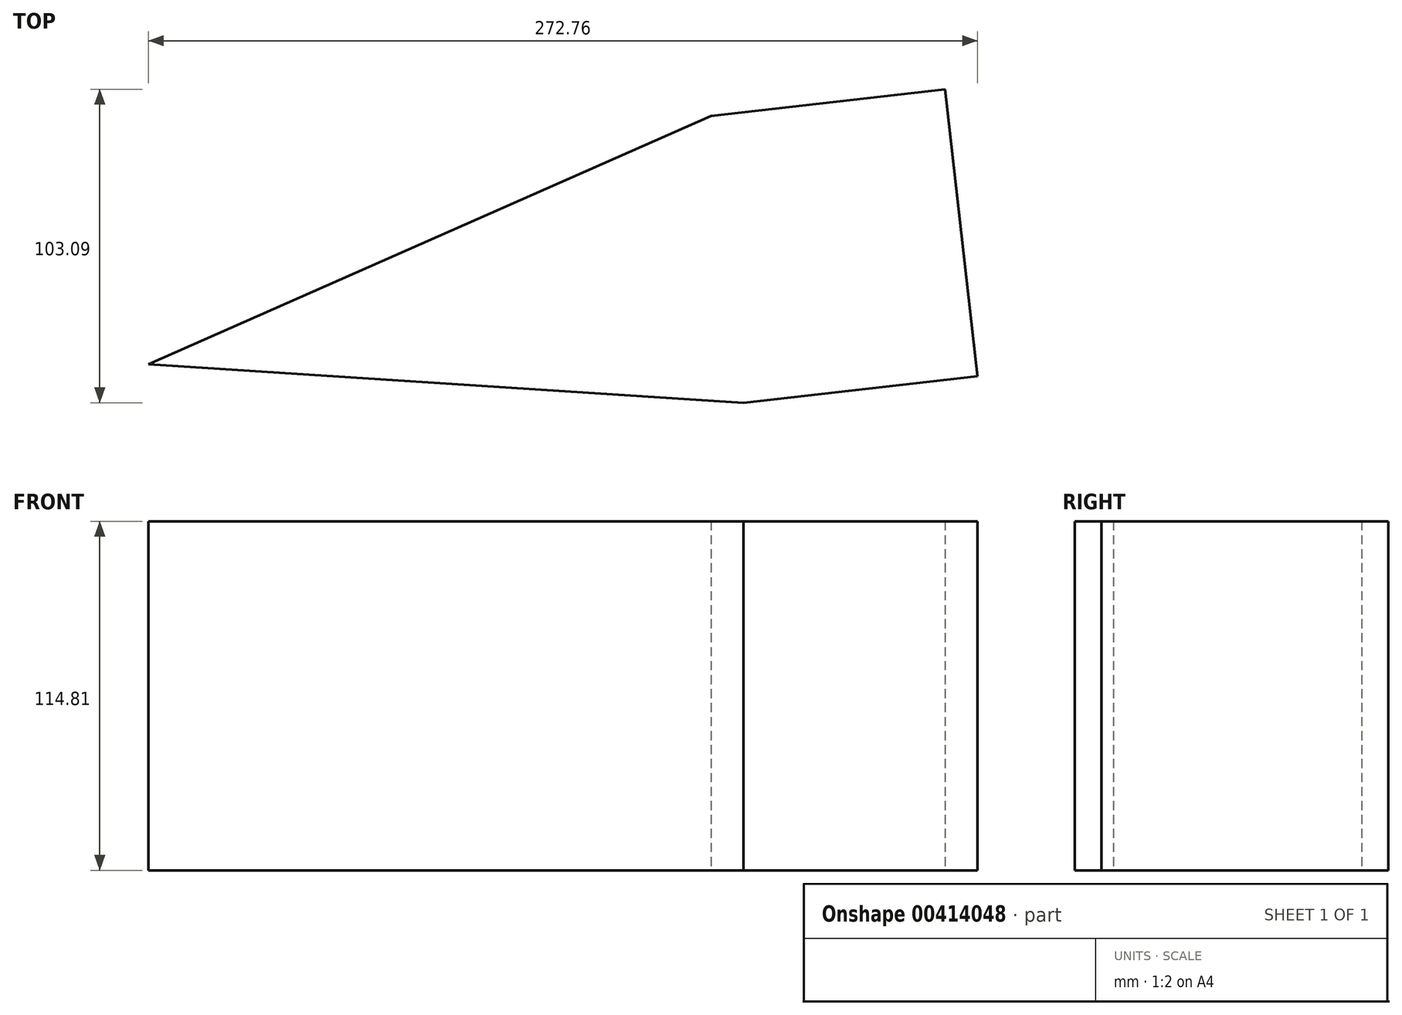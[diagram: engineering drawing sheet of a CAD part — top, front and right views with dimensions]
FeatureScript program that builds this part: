
annotation { "Feature Type Name" : "Feature", "Feature Type Description" : "" }
export const myFeature = defineFeature(function(context is Context, id is Id, definition is map)
    precondition{}
    {
        {
            var Q0;
            Q0=qCreatedBy(makeId("Top.planeOp"),FACE);
            var sketch = newSketch(context, id + "F0", { "sketchPlane" : qUnion([Q0])});
            skLineSegment(sketch, "E0", {"start": v(-49.68, -59.86) * mm, "end": v(135.38, 21.85) * mm});
            skLineSegment(sketch, "E1", {"start": v(135.38, 21.85) * mm, "end": v(146.1, -72.49) * mm});
            skLineSegment(sketch, "E2", {"start": v(146.1, -72.49) * mm, "end": v(-49.68, -59.86) * mm});
            skSolve(sketch);
        }
        {
            var Q0;
            Q0=makeQuery(id+"F0.imprint","IMPRINT",FACE,{"disambiguationData":[TD([[makeQuery(id+"F0.imprint","IMPRINT",EDGE,{"derivedFrom":sQuery(id+"F0.wireOp",EDGE,"E0")}),-1.0]])]});
            extrude(context, id + "F1", {"entities" : qUnion([Q0]), "depth" : 76.7 * mm});
        }
        {
            var Q0;
            Q0=makeQuery(id+"F1.opExtrude","SWEPT_FACE",FACE,{"disambiguationData":[OSD([sQuery(id+"F0.wireOp",EDGE,"E1")])]});
            extrude(context, id + "F2", {"entities" : qUnion([Q0]), "operationType" : NewBodyOperationType.ADD, "depth" : 77.47 * mm});
        }
        {
            var Q0;
            {var subQ0=sQuery(id+"F0.wireOp",EDGE,"E1");Q0=makeQuery(id+"F2.boolean.opBoolean","MERGE",FACE,{"derivedFrom":[makeQuery(id+"F1.opExtrude","CAP_FACE",FACE,{"disambiguationData":[OSD([sQuery(id+"F0.wireOp",EDGE,"E0"),subQ0,sQuery(id+"F0.wireOp",EDGE,"E2")])],"isStart":false}),makeQuery(id+"F2.opExtrude","SWEPT_FACE",FACE,{"disambiguationData":[OSD([subQ0]),TDD([makeQuery(id+"F1.opExtrude","CAP_EDGE",EDGE,{"disambiguationData":[OSD([subQ0])],"isStart":false})])]})]});}
            extrude(context, id + "F3", {"entities" : qUnion([Q0]), "operationType" : NewBodyOperationType.ADD, "depth" : 38.1 * mm});
        }
    });
